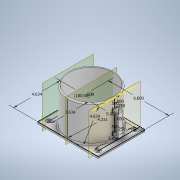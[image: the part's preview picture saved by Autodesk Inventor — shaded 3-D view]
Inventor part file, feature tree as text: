
AUTODESK INVENTOR PART (.ipt)
format: ipt  version: 2020 (Build 240168000, 168)  size: 450,048 bytes
history: native  units: in
note: dims shown in document units (in); Inventor stores cm internally (conversion verified against a paired STEP export)
features: extrude x6, sketch x4, plane x3, fillet x2, hole x1, mirror x1
ambient origin geometry x8: Origin, YZ Plane, XZ Plane, XY Plane, X Axis, Y Axis, Z Axis, Center Point
bodies: Solid1 (feature_tree)
feature tree (17):
  sketch  "Sketch1"  dims[d0=6.0in d1=4.6339in]
  extrude  "Extrusion1"  Depth=4.6339in
  extrude  "Extrusion2"  TaperAngle=180.0deg  [1 undecoded]
  hole  "Hole1"  [1 undecoded]
  extrude  "Extrusion3"  Depth=0.0625in
  plane  "Work Plane1"
  plane  "Work Plane2"
  sketch  "Sketch3"  dims[d5=5.0in d6=0.5in]
  extrude  "Extrusion4"  Depth=0.0625in
  extrude  "Extrusion5"  Depth=0.0625in
  extrude  "Extrusion6"  Depth=0.0625in TaperAngle=0.0deg
  fillet  "Fillet1"  Radius=0.1875in
  fillet  "Fillet2"  Radius=0.5in
  plane  "Work Plane3"
  mirror  "Mirror2"
  sketch  "Sketch2"  dims[d3=0.5in d4=180.0deg]
  sketch  "Sketch5"  dims[d7=3.634in d8=3.634in d9=4.3307in d10=4.6339in d11=3.5433in d12=0.0in d13=0.1875in d14=0.0in d15=0.266in d16=0.625in d17=0.507in d18=0.25in d19=0.5635in d20=1.0in d21=0.8108in d22=0.5in d23=0.5in d24=0.5in d25=0.5in d26=0.0625in d27=0.0in d28=1.0in d29=0.25in d30=0.5in d31=2.0in d32=0.25in d33=0.5in d34=0.125in d35=0.0in d36=0.375in d37=0.0in d38=0.25in d39=0.0in d40=0.0625in d41=0.125in]
note: 2 required parameter values undecoded (feature->parameter linkage not recoverable at this tier; creation-order binding heuristic only, values carry confidence <= 0.55)
